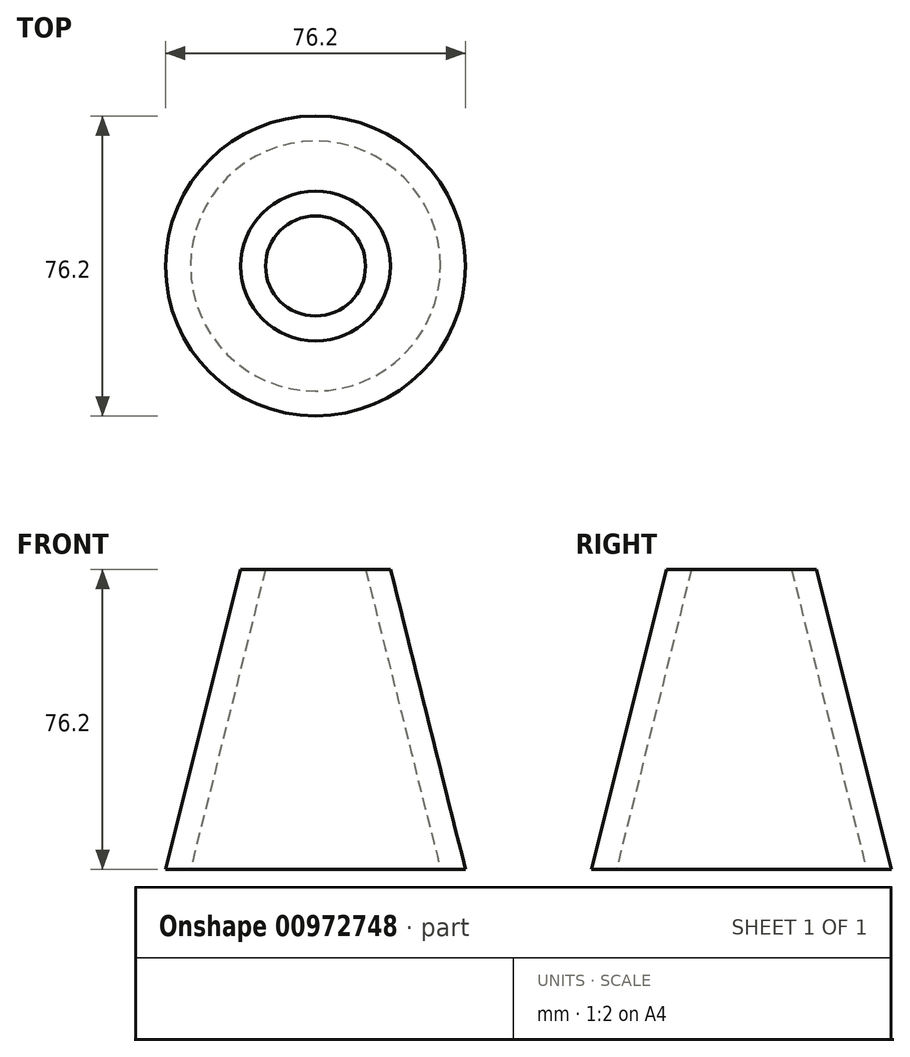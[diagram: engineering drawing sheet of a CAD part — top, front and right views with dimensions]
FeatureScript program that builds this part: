
annotation { "Feature Type Name" : "Feature", "Feature Type Description" : "" }
export const myFeature = defineFeature(function(context is Context, id is Id, definition is map)
    precondition{}
    {
        {
            var Q0;
            Q0=qCreatedBy(makeId("Front.planeOp"),FACE);
            var sketch = newSketch(context, id + "F0", { "sketchPlane" : qUnion([Q0])});
            skLineSegment(sketch, "E0", {"start": v(0, 0) * mm, "end": v(-6.35, 0) * mm});
            skLineSegment(sketch, "E1", {"start": v(12.7, 76.2) * mm, "end": v(-6.35, 0) * mm});
            skLineSegment(sketch, "E2", {"start": v(12.7, 76.2) * mm, "end": v(19.05, 76.2) * mm});
            skLineSegment(sketch, "E3", {"start": v(31.75, 76.2) * mm, "end": v(31.75, 0) * mm});
            skLineSegment(sketch, "E4", {"start": v(19.05, 76.2) * mm, "end": v(0, 0) * mm});
            skSolve(sketch);
        }
        {
            var Q0;
            Q0=makeQuery(id+"F0.imprint","IMPRINT",FACE,{"disambiguationData":[TD([[makeQuery(id+"F0.imprint","IMPRINT",EDGE,{"derivedFrom":sQuery(id+"F0.wireOp",EDGE,"E0")}),-1.0]])]});
            var Q1;
            Q1=sQuery(id+"F0.wireOp",EDGE,"E3");
            revolve(context, id + "F1", {"surfaceOperationType" : NewSurfaceOperationType.NEW, "entities" : qUnion([Q0]), "axis" : qUnion([Q1]), "revolveType" : RevolveType.FULL});
        }
    });
